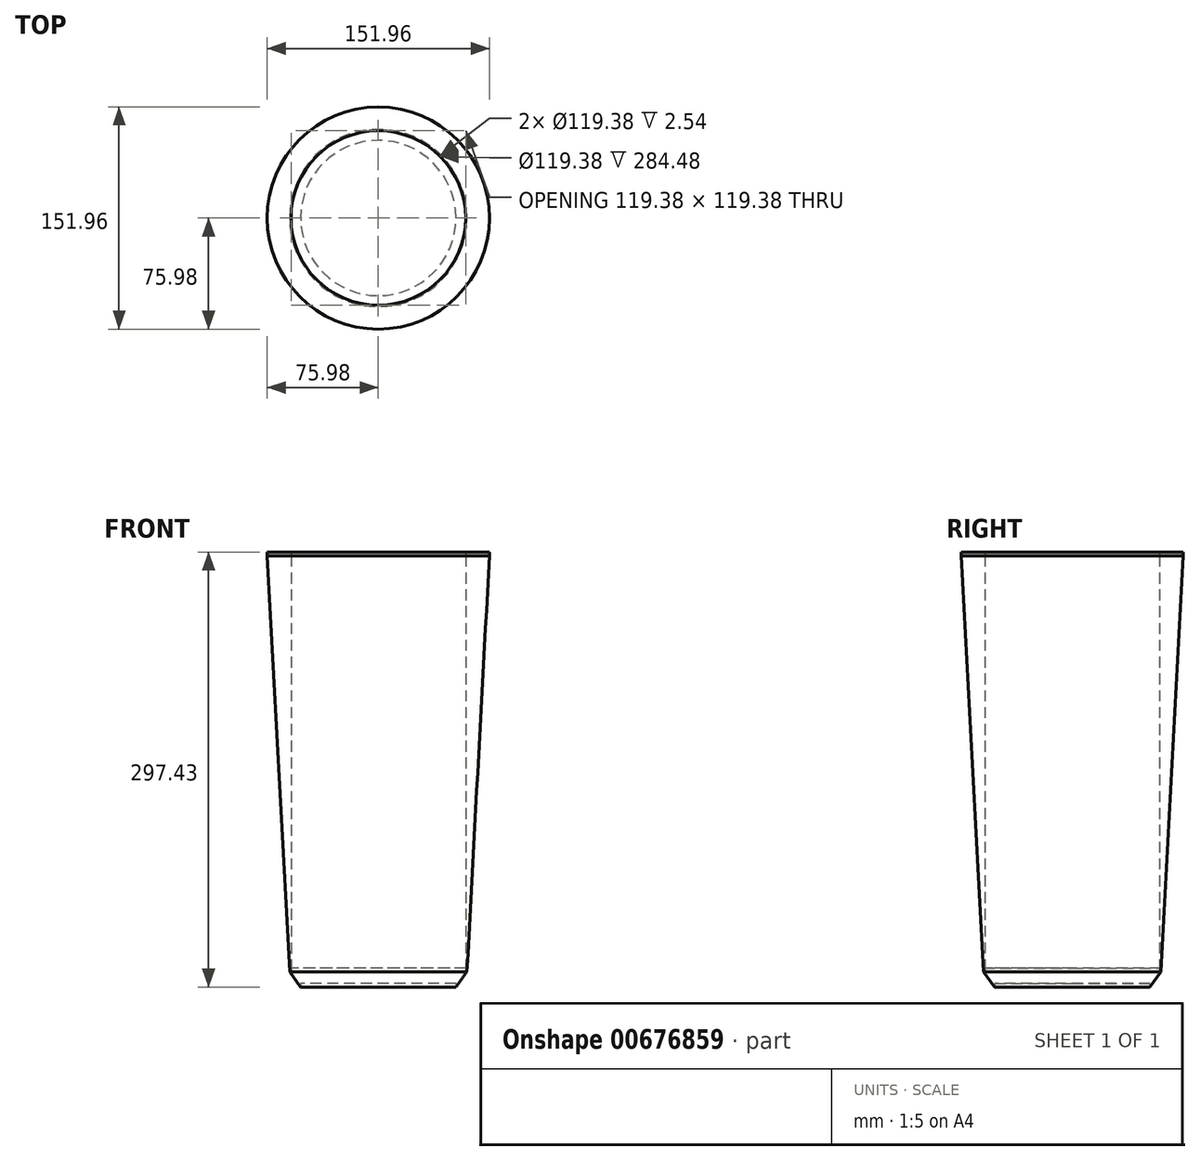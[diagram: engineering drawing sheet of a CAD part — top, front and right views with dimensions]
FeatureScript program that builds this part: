
annotation { "Feature Type Name" : "Feature", "Feature Type Description" : "" }
export const myFeature = defineFeature(function(context is Context, id is Id, definition is map)
    precondition{}
    {
        {
            var Q0;
            Q0=qCreatedBy(makeId("Top.planeOp"),FACE);
            cPlane(context, id + "F0", {"entities" : qUnion([Q0]), "cplaneType" : CPlaneType.OFFSET, "offset" : 284.48 * mm, "width" : 152.4 * mm, "height" : 152.4 * mm});
        }
        {
            var Q0;
            Q0=qCreatedBy(id+"F0.planeOp",FACE);
            var sketch = newSketch(context, id + "F1", { "sketchPlane" : qUnion([Q0])});
            skCircle(sketch, "E0", {"center": v(0, 0) * mm, "radius": 75.98 * mm});
            skSolve(sketch);
        }
        {
            var Q0;
            Q0 = qSketchRegion(id + "F1", true);
            extrude(context, id + "F2", {"entities" : qUnion([Q0]), "depth" : 2.54 * mm, "offsetDistance" : 25.4 * mm});
        }
        {
            var Q0;
            Q0=qCreatedBy(makeId("Top.planeOp"),FACE);
            var sketch = newSketch(context, id + "F3", { "sketchPlane" : qUnion([Q0])});
            skCircle(sketch, "E1", {"center": v(0, 0) * mm, "radius": 60.62 * mm});
            skSolve(sketch);
        }
        {
            var Q0;
            Q0 = qSketchRegion(id + "F3", true);
            extrude(context, id + "F4", {"entities" : qUnion([Q0]), "depth" : 2.54 * mm, "offsetDistance" : 25.4 * mm});
        }
        {
            var Q0;
            Q0 = qSketchRegion(id + "F1", true);
            var Q1;
            Q1 = qSketchRegion(id + "F3", true);
            loft(context, id + "F5", {"sheetProfilesArray" : [{ "sheetProfileEntities" : qUnion([Q0]) }, { "sheetProfileEntities" : qUnion([Q1]) }]});
        }
        {
            var Q0;
            Q0=sQuery(id+"F3.wireOp",VERTEX,"E1.center");
            var Q1;
            Q1=makeQuery(id+"F4.opExtrude","SWEPT_BODY",BODY,{"disambiguationData":[OSD([sQuery(id+"F3.wireOp",EDGE,"E1")])]});
            var Q2;
            Q2=makeQuery(id+"F5.opLoft","SWEPT_BODY",BODY,{"disambiguationData":[OSD([makeQuery(id+"F1.imprint","IMPRINT",FACE,{"disambiguationData":[TD([[makeQuery(id+"F1.imprint","IMPRINT",EDGE,{"derivedFrom":sQuery(id+"F1.wireOp",EDGE,"E0")}),1.0]])]}),makeQuery(id+"F3.imprint","IMPRINT",FACE,{"disambiguationData":[TD([[makeQuery(id+"F3.imprint","IMPRINT",EDGE,{"derivedFrom":sQuery(id+"F3.wireOp",EDGE,"E1")}),1.0]])]})])]});
            var Q3;
            Q3=makeQuery(id+"F2.opExtrude","SWEPT_BODY",BODY,{"disambiguationData":[OSD([sQuery(id+"F1.wireOp",EDGE,"E0")])]});
            hole(context, id + "F6", {"style" : HoleStyle.SIMPLE, "endStyle" : HoleEndStyle.THROUGH, "oppositeDirection" : true, "holeDiameter" : 119.38 * mm, "majorDiameter" : 6.35 * mm, "isTappedThrough" : true, "tappedDepth" : 12.7 * mm, "tapClearance" : 3, "locations" : qUnion([Q0]), "scope" : qUnion([Q1, Q2, Q3])});
        }
        {
            var Q0;
            Q0=qCreatedBy(makeId("Top.planeOp"),FACE);
            cPlane(context, id + "F7", {"entities" : qUnion([Q0]), "cplaneType" : CPlaneType.OFFSET, "offset" : 10.4 * mm, "oppositeDirection" : true, "width" : 152.4 * mm, "height" : 152.4 * mm});
        }
        {
            var Q0;
            Q0=qCreatedBy(id+"F7.planeOp",FACE);
            var sketch = newSketch(context, id + "F8", { "sketchPlane" : qUnion([Q0])});
            skCircle(sketch, "E2", {"center": v(0, 0) * mm, "radius": 53.08 * mm});
            skSolve(sketch);
        }
        {
            var Q0;
            Q0 = qSketchRegion(id + "F8", true);
            extrude(context, id + "F9", {"entities" : qUnion([Q0]), "depth" : 2.54 * mm, "offsetDistance" : 25.4 * mm});
        }
        {
            var Q0;
            Q0 = qSketchRegion(id + "F8", true);
            var Q1;
            Q1 = qSketchRegion(id + "F3", true);
            loft(context, id + "F10", {"sheetProfilesArray" : [{ "sheetProfileEntities" : qUnion([Q0]) }, { "sheetProfileEntities" : qUnion([Q1]) }]});
        }
    });
